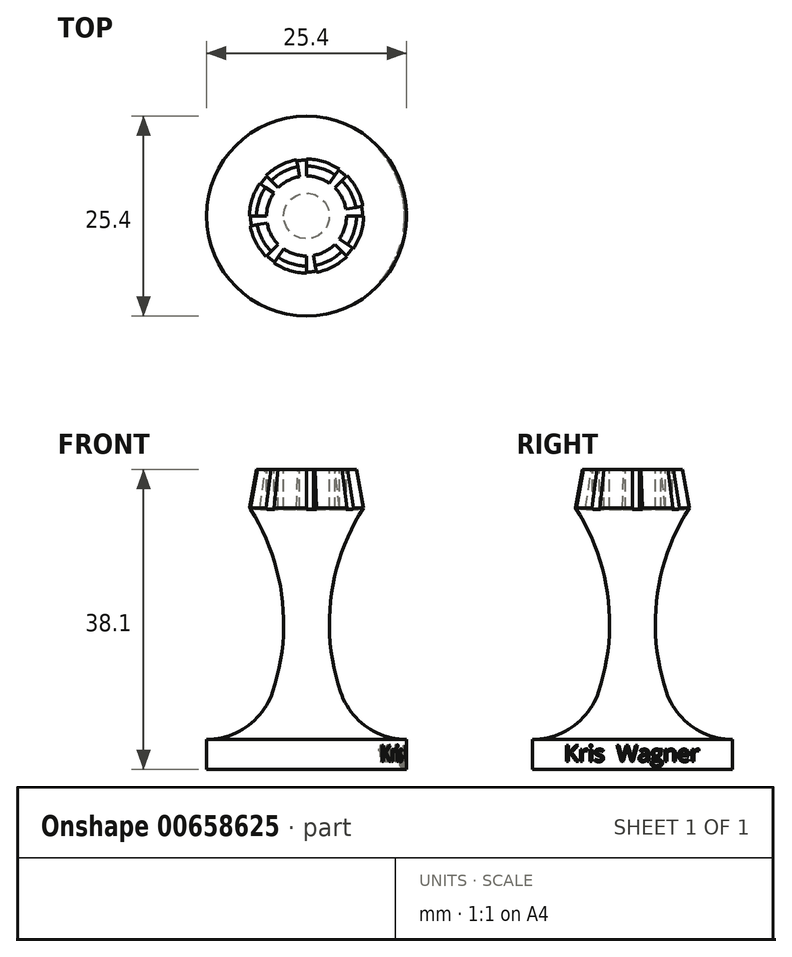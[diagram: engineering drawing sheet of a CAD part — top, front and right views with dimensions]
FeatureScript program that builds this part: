
annotation { "Feature Type Name" : "Feature", "Feature Type Description" : "" }
export const myFeature = defineFeature(function(context is Context, id is Id, definition is map)
    precondition{}
    {
        {
            var Q0;
            Q0=qCreatedBy(makeId("Front.planeOp"),FACE);
            var sketch = newSketch(context, id + "F0", { "sketchPlane" : qUnion([Q0])});
            skLineSegment(sketch, "E0.bottom", {"start": v(0, 0) * mm, "end": v(12.7, 0) * mm, "construction": true});
            skLineSegment(sketch, "E0.top", {"start": v(0, 38.1) * mm, "end": v(12.7, 38.1) * mm, "construction": true});
            skLineSegment(sketch, "E0.left", {"start": v(0, 0) * mm, "end": v(0, 38.1) * mm, "construction": true});
            skLineSegment(sketch, "E0.right", {"start": v(12.7, 0) * mm, "end": v(12.7, 38.1) * mm, "construction": true});
            skLineSegment(sketch, "E1", {"start": v(0, 0) * mm, "end": v(12.7, 0) * mm});
            skLineSegment(sketch, "E2", {"start": v(12.7, 0) * mm, "end": v(12.7, 3.81) * mm});
            skPoint(sketch, "E3", {"position": v(0, 19.05) * mm});
            skPoint(sketch, "E4", {"position": v(12.7, 19.05) * mm});
            skArc(sketch, "E5", {"start": v(4.3, 9.85) * mm, "mid": v(7.53, 5.48) * mm, "end": v(12.7, 3.8) * mm});
            skArc(sketch, "E6", {"start": v(7.25, 33.24) * mm, "mid": v(3.12, 21.88) * mm, "end": v(4.3, 9.85) * mm});
            skLineSegment(sketch, "E7", {"start": v(7.25, 33.24) * mm, "end": v(6.35, 38.1) * mm});
            skLineSegment(sketch, "E8", {"start": v(6.35, 38.1) * mm, "end": v(0, 38.1) * mm});
            skLineSegment(sketch, "E9", {"start": v(7.25, 33.24) * mm, "end": v(12.7, 3.81) * mm, "construction": true});
            skLineSegment(sketch, "E10", {"start": v(0, 38.1) * mm, "end": v(0, 0) * mm});
            skLineSegment(sketch, "E11", {"start": v(11.56, 9.95) * mm, "end": v(10.64, 14.94) * mm});
            skArc(sketch, "E12", {"start": v(10.64, 14.94) * mm, "mid": v(8.6, 11.98) * mm, "end": v(11.56, 9.95) * mm});
            skLineSegment(sketch, "E13", {"start": v(9.05, 23.52) * mm, "end": v(9.98, 18.52) * mm});
            skArc(sketch, "E14", {"start": v(9.05, 23.52) * mm, "mid": v(7.02, 20.56) * mm, "end": v(9.98, 18.52) * mm});
            skSolve(sketch);
        }
        {
            var Q0;
            Q0=makeQuery(id+"F0.imprint","IMPRINT",FACE,{"disambiguationData":[TD([[makeQuery(id+"F0.imprint","IMPRINT",EDGE,{"derivedFrom":sQuery(id+"F0.wireOp",EDGE,"E1")}),1.0]])]});
            var Q1;
            Q1=sQuery(id+"F0.wireOp",EDGE,"E0.left");
            revolve(context, id + "F1", {"entities" : qUnion([Q0]), "axis" : qUnion([Q1]), "revolveType" : RevolveType.FULL});
        }
        {
            var Q0;
            Q0=sQuery(id+"F0.wireOp",EDGE,"E1");
            var Q1;
            Q1=sQuery(id+"F0.wireOp",VERTEX,"E2.start");
            cPlane(context, id + "F2", {"entities" : qUnion([Q0, Q1]), "cplaneType" : CPlaneType.LINE_POINT, "offset" : 25.4 * mm, "width" : 152.4 * mm, "height" : 152.4 * mm});
        }
        {
            var Q0;
            Q0=qCreatedBy(id+"F2.planeOp",FACE);
            var sketch = newSketch(context, id + "F3", { "sketchPlane" : qUnion([Q0])});
            skLineSegment(sketch, "E15", {"start": v(-12.7, 0) * mm, "end": v(-12.7, 2.54) * mm});
            skText(sketch, "E16", { "text": "Kris  Wagner", "fontName": "OpenSans-Regular.ttf"});
            const initialGuessF3  = {"E16": [-0.00864, 0.001, 1, 0, 0.0021]};
            skSetInitialGuess(sketch, initialGuessF3);
            skSolve(sketch);
        }
        {
            var Q0;
            Q0 = qSketchRegion(id + "F3", true);
            var Q1;
            Q1=makeQuery(id+"F1.opRevolve","SWEPT_FACE",FACE,{"disambiguationData":[OSD([sQuery(id+"F0.wireOp",EDGE,"E2")])]});
            extrude(context, id + "F4", {"entities" : qUnion([Q0]), "operationType" : NewBodyOperationType.REMOVE, "endBound" : BoundingType.UP_TO_SURFACE, "oppositeDirection" : true, "depth" : 25.4 * mm, "endBoundEntityFace" : qUnion([Q1]), "hasOffset" : true, "offsetDistance" : -0.25 * mm});
        }
        {
            var Q0;
            Q0=makeQuery(id+"F1.opRevolve","SWEPT_FACE",FACE,{"disambiguationData":[OSD([sQuery(id+"F0.wireOp",EDGE,"E8")])]});
            var sketch = newSketch(context, id + "F5", { "sketchPlane" : qUnion([Q0])});
            skArc(sketch, "E17.0", {"start": v(1.26, -7.14) * mm, "mid": v(0.63, -7.22) * mm, "end": v(0, -7.25) * mm});
            skCircle(sketch, "E18", {"center": v(0, 0) * mm, "radius": 5.08 * mm});
            skLineSegment(sketch, "E19", {"start": v(0, -5.08) * mm, "end": v(0, -7.25) * mm});
            skLineSegment(sketch, "E20", {"start": v(0.88, -5) * mm, "end": v(1.26, -7.14) * mm});
            skLineSegment(sketch, "E21.anchor1", {"start": v(0, 0) * mm, "end": v(0, -7.25) * mm, "construction": true});
            skLineSegment(sketch, "E21.anchor2", {"start": v(0, 0) * mm, "end": v(0, -7.25) * mm, "construction": true});
            skLineSegment(sketch, "E22.1.0", {"start": v(4.16, -2.91) * mm, "end": v(5.94, -4.16) * mm});
            skArc(sketch, "E22.1.1", {"start": v(5.94, -4.16) * mm, "mid": v(5.55, -4.66) * mm, "end": v(5.13, -5.13) * mm});
            skLineSegment(sketch, "E22.1.2", {"start": v(3.6, -3.6) * mm, "end": v(5.13, -5.13) * mm});
            skLineSegment(sketch, "E22.2.0", {"start": v(5, 0.88) * mm, "end": v(7.14, 1.26) * mm});
            skArc(sketch, "E22.2.1", {"start": v(7.14, 1.26) * mm, "mid": v(7.22, 0.63) * mm, "end": v(7.25, 0) * mm});
            skLineSegment(sketch, "E22.2.2", {"start": v(5.08, 0) * mm, "end": v(7.25, 0) * mm});
            skLineSegment(sketch, "E22.3.0", {"start": v(2.91, 4.16) * mm, "end": v(4.16, 5.94) * mm});
            skArc(sketch, "E22.3.1", {"start": v(4.16, 5.94) * mm, "mid": v(4.66, 5.55) * mm, "end": v(5.13, 5.13) * mm});
            skLineSegment(sketch, "E22.3.2", {"start": v(3.6, 3.6) * mm, "end": v(5.13, 5.13) * mm});
            skLineSegment(sketch, "E22.4.0", {"start": v(-0.88, 5) * mm, "end": v(-1.26, 7.14) * mm});
            skArc(sketch, "E22.4.1", {"start": v(-1.26, 7.14) * mm, "mid": v(-0.63, 7.22) * mm, "end": v(0, 7.25) * mm});
            skLineSegment(sketch, "E22.4.2", {"start": v(0, 5.08) * mm, "end": v(0, 7.25) * mm});
            skLineSegment(sketch, "E22.5.0", {"start": v(-4.16, 2.91) * mm, "end": v(-5.94, 4.16) * mm});
            skArc(sketch, "E22.5.1", {"start": v(-5.94, 4.16) * mm, "mid": v(-5.55, 4.66) * mm, "end": v(-5.13, 5.13) * mm});
            skLineSegment(sketch, "E22.5.2", {"start": v(-3.6, 3.6) * mm, "end": v(-5.13, 5.13) * mm});
            skLineSegment(sketch, "E22.6.0", {"start": v(-5, -0.88) * mm, "end": v(-7.14, -1.26) * mm});
            skArc(sketch, "E22.6.1", {"start": v(-7.14, -1.26) * mm, "mid": v(-7.22, -0.63) * mm, "end": v(-7.25, 0) * mm});
            skLineSegment(sketch, "E22.6.2", {"start": v(-5.08, 0) * mm, "end": v(-7.25, 0) * mm});
            skLineSegment(sketch, "E22.7.0", {"start": v(-2.91, -4.16) * mm, "end": v(-4.16, -5.94) * mm});
            skArc(sketch, "E22.7.1", {"start": v(-4.16, -5.94) * mm, "mid": v(-4.66, -5.55) * mm, "end": v(-5.13, -5.13) * mm});
            skLineSegment(sketch, "E22.7.2", {"start": v(-3.6, -3.6) * mm, "end": v(-5.13, -5.13) * mm});
            skSolve(sketch);
        }
        {
            var Q0;
            Q0 = qSketchRegion(id + "F5", true);
            extrude(context, id + "F6", {"entities" : qUnion([Q0]), "operationType" : NewBodyOperationType.REMOVE, "oppositeDirection" : true, "depth" : 5.08 * mm, "offsetDistance" : 25.4 * mm});
        }
    });
